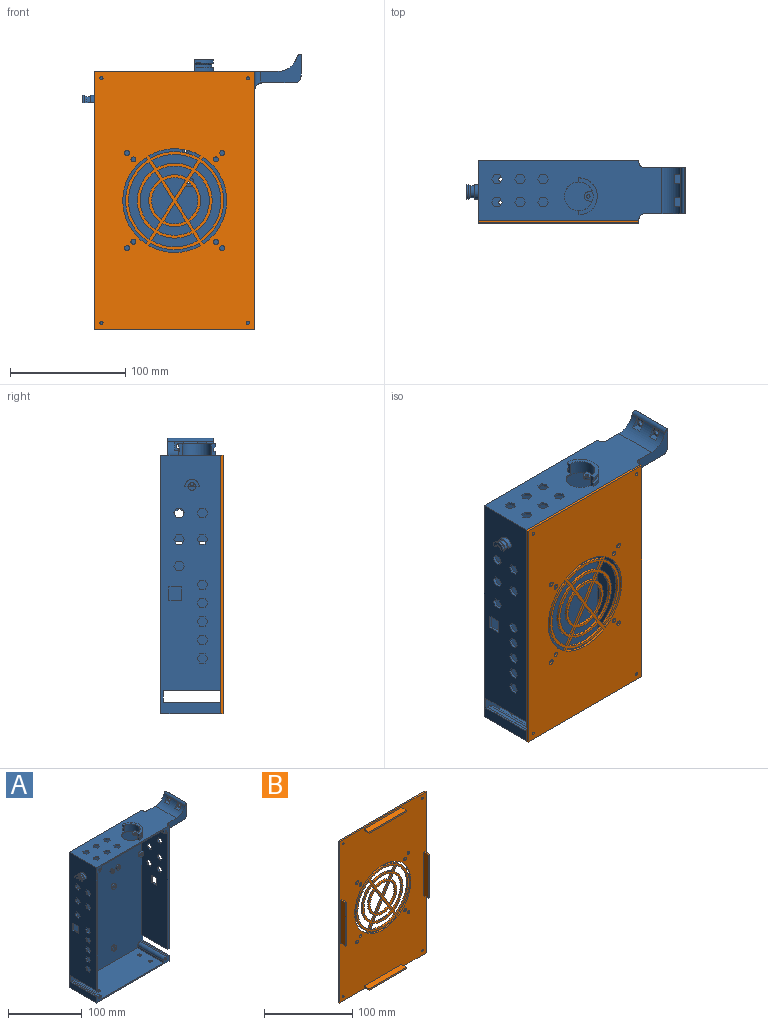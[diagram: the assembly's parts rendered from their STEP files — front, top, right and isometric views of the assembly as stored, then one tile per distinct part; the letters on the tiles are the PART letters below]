
ASSEMBLY  parts=2 mates=1
PART A: 292 faces, bbox 189x52x239 mm
  f0: cylinder r=17.13mm len=40mm, axis (0,-1,0), area 731mm2, adj f15,f134,f136,f139,f146,f147,f148,f149
  f1: plane 224x52mm, normal (1,0,0), area 9895.4mm2, adj f4,f7,f15,f16,f20,f21,f103,f104
  f2: plane 224x52mm, normal (-1,0,0), area 10383.8mm2, adj f4,f7,f11,f12,f15,f16,f20,f21
  f3: plane 193.92x50mm, normal (1,0,0), area 8938.3mm2, adj f16,f20,f28,f29,f32,f33,f36,f37
  f4: plane 224x139mm, normal (0,1,0), area 31065.2mm2, adj f1,f2,f15,f21,f22,f25,f31,f35
  f5: plane 50x0.08mm, normal (-1,0,0), area 3.8mm2, adj f7,f16,f70,f103
  f6: plane 50x0.08mm, normal (1,0,0), area 3.8mm2, adj f7,f16,f72,f105
  f7: plane 139x10.08mm, normal (0,-1,0), area 416.1mm2, adj f1,f2,f5,f6,f17,f21,f70,f71
  f8: cylinder r=3.25mm len=10mm, axis (-1,0,0), area 40.4mm2, adj f11,f96,f101,f102
  f9: cylinder r=3.25mm len=10mm, axis (-1,0,0), area 40.4mm2, adj f12,f96,f101,f102
  f10: cylinder r=6.25mm len=12.5mm, axis (1,0,0), area 33.7mm2, adj f11,f12,f96,f99
  f11: plane 10x3mm, normal (0,0,-1), area 26.3mm2, adj f2,f8,f10,f95,f96,f97,f98,f99
  f12: plane 10x3mm, normal (0,0,-1), area 26.3mm2, adj f2,f9,f10,f95,f96,f97,f98,f99
  f13: cylinder r=12.5mm len=25mm, axis (0,0,1), area 534.6mm2, adj f15,f19,f82,f83,f85,f89,f90,f91
  f14: cylinder r=16mm len=32mm, axis (0,0,-1), area 175.9mm2, adj f15,f82,f83,f86
  f15: plane 159x52mm, normal (0,0,1), area 7060.9mm2, adj f0,f1,f2,f4,f13,f14,f20,f82
  f16: plane 220x139mm, normal (0,-1,0), area 29004.3mm2, adj f1,f2,f3,f5,f6,f17,f18,f19
  f17: plane 119x50mm, normal (0,0,1), area 5871.5mm2, adj f7,f16,f71,f73,f288,f289,f290,f291
  f18: plane 193.92x50mm, normal (-1,0,0), area 9201.6mm2, adj f16,f20,f56,f59,f60,f61,f62,f65
  f19: plane 119x50mm, normal (0,0,-1), area 5173.4mm2, adj f13,f16,f20,f67,f69,f89,f90,f92
  f20: plane 203.92x139mm, normal (0,-1,0), area 1191.5mm2, adj f1,f2,f3,f15,f18,f19,f66,f67
  f21: plane 139x52mm, normal (0,0,-1), area 7149.5mm2, adj f1,f2,f4,f7,f288,f289,f290,f291
  f22: cylinder r=1.35mm len=5mm, axis (0,1,0), area 42.4mm2, adj f4,f24
  f23: cylinder r=4mm len=8mm, axis (0,1,0), area 75.4mm2, adj f16,f24
  f24: plane 8x8mm, normal (0,-1,0), area 44.5mm2, adj f22,f23
  f25: cylinder r=1.35mm len=5mm, axis (0,1,0), area 42.4mm2, adj f4,f27
  f26: cylinder r=4mm len=8mm, axis (0,1,0), area 75.4mm2, adj f16,f27
  f27: plane 8x8mm, normal (0,-1,0), area 44.5mm2, adj f25,f26
  f28: plane 5x3mm, normal (0,0,1), area 15mm2, adj f3,f16,f32,f128
  f29: plane 5x3mm, normal (0,0,-1), area 15mm2, adj f3,f16,f32,f129
  f30: plane 3x2mm, normal (1,0,0), area 6mm2, adj f16,f32,f128,f129
  f31: cylinder r=1.35mm len=5mm, axis (0,1,0), area 42.4mm2, adj f4,f32
  f32: plane 8x8mm, normal (0,-1,0), area 54.4mm2, adj f3,f28,f29,f30,f31,f128,f129
  f33: plane 5x3mm, normal (0,0,-1), area 15mm2, adj f3,f16,f37,f127
  f34: plane 3x2mm, normal (1,0,0), area 6mm2, adj f16,f37,f126,f127
  f35: cylinder r=1.35mm len=5mm, axis (0,1,0), area 42.4mm2, adj f4,f37
  f36: plane 5x3mm, normal (0,0,1), area 15mm2, adj f3,f16,f37,f126
  f37: plane 8x8mm, normal (0,-1,0), area 54.4mm2, adj f3,f33,f34,f35,f36,f126,f127
  f38: cylinder r=1.35mm len=5mm, axis (0,1,0), area 42.4mm2, adj f4,f40
  f39: cylinder r=3mm len=6mm, axis (0,1,0), area 56.5mm2, adj f16,f40
  f40: plane 6x6mm, normal (0,-1,0), area 22.5mm2, adj f38,f39
  f41: cylinder r=1.35mm len=5mm, axis (0,1,0), area 42.4mm2, adj f4,f43
  f42: cylinder r=3mm len=6mm, axis (0,1,0), area 56.5mm2, adj f16,f43
  f43: plane 6x6mm, normal (0,-1,0), area 22.5mm2, adj f41,f42
  f44: cylinder r=1.35mm len=5mm, axis (0,1,0), area 42.4mm2, adj f4,f46
  f45: cylinder r=3mm len=6mm, axis (0,1,0), area 56.5mm2, adj f16,f46
  f46: plane 6x6mm, normal (0,-1,0), area 22.5mm2, adj f44,f45
  f47: cylinder r=1.35mm len=5mm, axis (0,1,0), area 42.4mm2, adj f4,f49
  f48: cylinder r=3mm len=6mm, axis (0,1,0), area 56.5mm2, adj f16,f49
  f49: plane 6x6mm, normal (0,-1,0), area 22.5mm2, adj f47,f48
  f50: cylinder r=1.35mm len=5mm, axis (0,1,0), area 42.4mm2, adj f4,f52
  f51: cylinder r=3.5mm len=7mm, axis (0,1,0), area 66mm2, adj f16,f52
  f52: plane 7x7mm, normal (0,-1,0), area 32.8mm2, adj f50,f51
  f53: cylinder r=1.35mm len=5mm, axis (0,1,0), area 42.4mm2, adj f4,f55
  f54: cylinder r=3.5mm len=7mm, axis (0,1,0), area 66mm2, adj f16,f55
  f55: plane 7x7mm, normal (0,-1,0), area 32.8mm2, adj f53,f54
  f56: plane 4x3mm, normal (0,0,1), area 12mm2, adj f16,f18,f60,f125
  f57: plane 3x1mm, normal (-1,0,0), area 3mm2, adj f16,f60,f124,f125
  f58: cylinder r=1.35mm len=3mm, axis (0,1,0), area 25.4mm2, adj f60,f117
  f59: plane 4x3mm, normal (0,0,-1), area 12mm2, adj f16,f18,f60,f124
  f60: plane 7x7mm, normal (0,-1,0), area 39.4mm2, adj f18,f56,f57,f58,f59,f124,f125
  f61: plane 4x3mm, normal (0,0,-1), area 12mm2, adj f16,f18,f65,f122
  f62: plane 4x3mm, normal (0,0,1), area 12mm2, adj f16,f18,f65,f123
  f63: plane 3x1mm, normal (-1,0,0), area 3mm2, adj f16,f65,f122,f123
  f64: cylinder r=1.35mm len=5mm, axis (0,1,0), area 42.4mm2, adj f4,f65
  f65: plane 7x7mm, normal (0,-1,0), area 39.4mm2, adj f18,f61,f62,f63,f64,f122,f123
  f66: plane 50x3mm, normal (0,0,-1), area 150mm2, adj f3,f16,f20,f133
  f67: plane 50x3mm, normal (1,0,0), area 150mm2, adj f16,f19,f20,f133
  f68: plane 50x3mm, normal (0,0,-1), area 150mm2, adj f16,f18,f20,f132
  f69: plane 50x3mm, normal (-1,0,0), area 150mm2, adj f16,f19,f20,f132
  f70: plane 50x3mm, normal (0,0,1), area 150mm2, adj f5,f7,f16,f131
  f71: plane 50x3mm, normal (-1,0,0), area 150mm2, adj f7,f16,f17,f131
  f72: plane 50x3mm, normal (0,0,1), area 150mm2, adj f6,f7,f16,f130
  f73: plane 50x3mm, normal (1,0,0), area 150mm2, adj f7,f16,f17,f130
  f74: cylinder r=1.35mm len=25mm, axis (0,-1,0), area 212.1mm2, adj f20,f75
  f75: plane 2.7x2.7mm, normal (0,-1,0), area 5.7mm2, adj f74
  f76: cylinder r=1.35mm len=25mm, axis (0,-1,0), area 212.1mm2, adj f7,f77
  f77: plane 2.7x2.7mm, normal (0,-1,0), area 5.7mm2, adj f76
  f78: cylinder r=1.35mm len=25mm, axis (0,-1,0), area 212.1mm2, adj f7,f79
  f79: plane 2.7x2.7mm, normal (0,-1,0), area 5.7mm2, adj f78
  f80: cylinder r=1.35mm len=25mm, axis (0,-1,0), area 212.1mm2, adj f20,f81
  f81: plane 2.7x2.7mm, normal (0,-1,0), area 5.7mm2, adj f80
  f82: plane 10x3.5mm, normal (-1,0,0), area 30.3mm2, adj f13,f14,f15,f84,f85,f86,f87,f88
  f83: plane 10x3.5mm, normal (-1,0,0), area 30.3mm2, adj f13,f14,f15,f84,f85,f86,f87,f88
  f84: cylinder r=16mm len=32mm, axis (0,0,-1), area 134.9mm2, adj f82,f83,f85,f87
  f85: plane 32x16.14mm, normal (0,0,1), area 155.3mm2, adj f13,f82,f83,f84
  f86: plane 32x16.14mm, normal (0,0,1), area 70.2mm2, adj f14,f82,f83,f88
  f87: revolved ~32x16.2mm, area 93.7mm2, adj f82,f83,f84,f88
  f88: revolved ~29.04x14.72mm, area 114.2mm2, adj f82,f83,f86,f87
  f89: plane 3.05x2mm, normal (0,1,0), area 6.1mm2, adj f13,f19,f91,f93
  f90: plane 3.05x2mm, normal (0,-1,0), area 6.1mm2, adj f13,f19,f91,f93
  f91: plane 8x7.71mm, normal (0,0,1), area 46mm2, adj f13,f89,f90,f92,f93
  f92: cylinder r=1.5mm len=3mm, axis (0,0,1), area 18.8mm2, adj f19,f91
  f93: cylinder r=4mm len=8mm, axis (0,0,1), area 25.1mm2, adj f19,f89,f90,f91
  f94: cylinder r=3.25mm len=6.5mm, axis (-1,0,0), area 20.4mm2, adj f2,f3,f100
  f95: cylinder r=6.25mm len=12.5mm, axis (1,0,0), area 73.6mm2, adj f2,f11,f12,f97
  f96: plane 12.5x6.25mm, normal (-1,0,0), area 44.4mm2, adj f8,f9,f10,f11,f12,f101
  f97: plane 12.5x6.25mm, normal (-1,0,0), area 18.1mm2, adj f11,f12,f95,f98
  f98: cylinder r=5.25mm len=10.5mm, axis (1,0,0), area 46.2mm2, adj f11,f12,f97,f99
  f99: cone r=5.25mm half-angle=30deg, axis (-1,0,0), area 36.1mm2, adj f10,f11,f12,f98
  f100: plane 6.5x2mm, normal (0,0,-1), area 13mm2, adj f3,f94,f102
  f101: cylinder r=1.5mm len=12mm, axis (-1,0,0), area 41.9mm2, adj f3,f8,f9,f96,f102
  f102: plane 6.5x3.08mm, normal (-1,0,0), area 9.9mm2, adj f8,f9,f100,f101
  f103: plane 50x2mm, normal (0,0,1), area 100mm2, adj f1,f5,f7,f16
  f104: plane 50x2mm, normal (0,0,-1), area 100mm2, adj f1,f16,f18,f20
  f105: plane 50x2mm, normal (0,0,1), area 100mm2, adj f2,f6,f7,f16
  f106: plane 50x2mm, normal (0,0,-1), area 100mm2, adj f2,f3,f16,f20
  f107: plane 12x2mm, normal (0,1,0), area 24mm2, adj f1,f18,f108,f110
  f108: plane 10x2mm, normal (0,0,1), area 20mm2, adj f1,f18,f107,f109
  f109: plane 12x2mm, normal (0,-1,0), area 24mm2, adj f1,f18,f108,f110
  f110: plane 10x2mm, normal (0,0,-1), area 20mm2, adj f1,f18,f107,f109
  f111: plane 2x1.71mm, normal (-0.17,0,0.99), area 3.5mm2, adj f4,f112,f116,f117
  f112: plane 2x1.63mm, normal (-0.94,0,0.35), area 3.5mm2, adj f4,f111,f113,f117
  f113: plane 2x1.33mm, normal (-0.77,0,-0.64), area 3.5mm2, adj f4,f112,f114,f117
  f114: plane 2x1.71mm, normal (0.17,0,-0.99), area 3.5mm2, adj f4,f113,f115,f117
  f115: plane 2x1.63mm, normal (0.94,0,-0.35), area 3.5mm2, adj f4,f114,f116,f117
  f116: plane 2x1.33mm, normal (0.77,0,0.64), area 3.5mm2, adj f4,f111,f115,f117
  f117: plane 3.41x3.25mm, normal (0,1,0), area 2.1mm2, adj f58,f111,f112,f113,f114,f115,f116
  f118: plane 12x2mm, normal (0,-1,0), area 24mm2, adj f2,f3,f119,f121
  f119: plane 11x2mm, normal (0,0,1), area 22mm2, adj f2,f3,f118,f120
  f120: plane 12x2mm, normal (0,1,0), area 24mm2, adj f2,f3,f119,f121
  f121: plane 11x2mm, normal (0,0,-1), area 22mm2, adj f2,f3,f118,f120
  f122: cylinder r=3mm len=3mm, axis (0,1,0), area 14.1mm2, adj f16,f61,f63,f65
  f123: cylinder r=3mm len=3mm, axis (0,-1,0), area 14.1mm2, adj f16,f62,f63,f65
  f124: cylinder r=3mm len=3mm, axis (0,-1,0), area 14.1mm2, adj f16,f57,f59,f60
  f125: cylinder r=3mm len=3mm, axis (0,1,0), area 14.1mm2, adj f16,f56,f57,f60
  f126: cylinder r=3mm len=3mm, axis (0,-1,0), area 14.1mm2, adj f16,f34,f36,f37
  f127: cylinder r=3mm len=3mm, axis (0,1,0), area 14.1mm2, adj f16,f33,f34,f37
  f128: cylinder r=3mm len=3mm, axis (0,1,0), area 14.1mm2, adj f16,f28,f30,f32
  f129: cylinder r=3mm len=3mm, axis (0,-1,0), area 14.1mm2, adj f16,f29,f30,f32
  f130: cylinder r=5mm len=50mm, axis (0,-1,0), area 392.7mm2, adj f7,f16,f72,f73
  f131: cylinder r=5mm len=50mm, axis (0,-1,0), area 392.7mm2, adj f7,f16,f70,f71
  f132: cylinder r=5mm len=50mm, axis (0,-1,0), area 392.7mm2, adj f16,f20,f68,f69
  f133: cylinder r=5mm len=50mm, axis (0,-1,0), area 392.7mm2, adj f16,f20,f66,f67
  f134: plane 35x25.08mm, normal (0,-1,0), area 446.7mm2, adj f0,f15,f135,f137,f138,f139,f140,f141
  f135: plane 40x28mm, normal (0,0,-1), area 1120mm2, adj f134,f136,f140,f141
  f136: plane 35x25.08mm, normal (0,1,0), area 446.7mm2, adj f0,f15,f135,f137,f138,f139,f140,f141
  f137: plane 40x19mm, normal (1,0,0), area 720.7mm2, adj f134,f136,f138,f141,f144,f145
  f138: plane 40x0.15mm, normal (0,0,1), area 6mm2, adj f134,f136,f137,f139
  f139: cylinder r=3.5mm len=40mm, axis (0,-1,0), area 181.2mm2, adj f0,f134,f136,f138
  f140: cylinder r=6mm len=50mm, axis (0,1,0), area 408.1mm2, adj f1,f134,f135,f136,f142,f143
  f141: cylinder r=6mm len=40mm, axis (0,-1,0), area 377mm2, adj f134,f135,f136,f137
  f142: cylinder r=5mm len=16mm, axis (0,0,-1), area 97.4mm2, adj f1,f15,f134,f140
  f143: cylinder r=5mm len=16mm, axis (0,0,1), area 97.4mm2, adj f1,f15,f136,f140
  f144: cylinder r=2.5mm len=5mm, axis (1,0,0), area 55mm2, adj f137,f155
  f145: cylinder r=2.5mm len=5mm, axis (1,0,0), area 55mm2, adj f137,f150
  f146: plane 8x0.15mm, normal (0,0,-1), area 1.2mm2, adj f0,f147,f149,f150
  f147: plane 8x5.5mm, normal (0,1,0), area 18.2mm2, adj f0,f146,f148,f150
  f148: plane 8x5.5mm, normal (0,0,1), area 44mm2, adj f0,f147,f149,f150
  f149: plane 8x5.5mm, normal (0,-1,0), area 18.2mm2, adj f0,f146,f148,f150
  f150: plane 8x8mm, normal (-1,0,0), area 44.4mm2, adj f145,f146,f147,f148,f149
  f151: plane 8x0.15mm, normal (0,0,-1), area 1.2mm2, adj f0,f152,f154,f155
  f152: plane 8x5.5mm, normal (0,1,0), area 18.2mm2, adj f0,f151,f153,f155
  f153: plane 8x5.5mm, normal (0,0,1), area 44mm2, adj f0,f152,f154,f155
  f154: plane 8x5.5mm, normal (0,-1,0), area 18.2mm2, adj f0,f151,f153,f155
  f155: plane 8x8mm, normal (-1,0,0), area 44.4mm2, adj f144,f151,f152,f153,f154
  f156: plane 4.62x2mm, normal (0,0,-1), area 9.2mm2, adj f1,f18,f157,f161
  f157: plane 4x2.31mm, normal (0,0.87,-0.5), area 9.2mm2, adj f1,f18,f156,f158
  f158: plane 4x2.31mm, normal (0,0.87,0.5), area 9.2mm2, adj f1,f18,f157,f159
  f159: plane 4.62x2mm, normal (0,0,1), area 9.2mm2, adj f1,f18,f158,f160
  f160: plane 4x2.31mm, normal (0,-0.87,0.5), area 9.2mm2, adj f1,f18,f159,f161
  f161: plane 4x2.31mm, normal (0,-0.87,-0.5), area 9.2mm2, adj f1,f18,f156,f160
  f162: plane 4.62x2mm, normal (0,0,-1), area 9.2mm2, adj f1,f18,f163,f167
  f163: plane 4x2.31mm, normal (0,0.87,-0.5), area 9.2mm2, adj f1,f18,f162,f164
  f164: plane 4x2.31mm, normal (0,0.87,0.5), area 9.2mm2, adj f1,f18,f163,f165
  f165: plane 4.62x2mm, normal (0,0,1), area 9.2mm2, adj f1,f18,f164,f166
  f166: plane 4x2.31mm, normal (0,-0.87,0.5), area 9.2mm2, adj f1,f18,f165,f167
  f167: plane 4x2.31mm, normal (0,-0.87,-0.5), area 9.2mm2, adj f1,f18,f162,f166
  f168: plane 4.62x2mm, normal (0,0,-1), area 9.2mm2, adj f1,f18,f169,f173
  f169: plane 4x2.31mm, normal (0,0.87,-0.5), area 9.2mm2, adj f1,f18,f168,f170
  f170: plane 4x2.31mm, normal (0,0.87,0.5), area 9.2mm2, adj f1,f18,f169,f171
  f171: plane 4.62x2mm, normal (0,0,1), area 9.2mm2, adj f1,f18,f170,f172
  f172: plane 4x2.31mm, normal (0,-0.87,0.5), area 9.2mm2, adj f1,f18,f171,f173
  f173: plane 4x2.31mm, normal (0,-0.87,-0.5), area 9.2mm2, adj f1,f18,f168,f172
  f174: plane 4.62x2mm, normal (0,0,-1), area 9.2mm2, adj f1,f18,f175,f179
  f175: plane 4x2.31mm, normal (0,0.87,-0.5), area 9.2mm2, adj f1,f18,f174,f176
  f176: plane 4x2.31mm, normal (0,0.87,0.5), area 9.2mm2, adj f1,f18,f175,f177
  f177: plane 4.62x2mm, normal (0,0,1), area 9.2mm2, adj f1,f18,f176,f178
  f178: plane 4x2.31mm, normal (0,-0.87,0.5), area 9.2mm2, adj f1,f18,f177,f179
  f179: plane 4x2.31mm, normal (0,-0.87,-0.5), area 9.2mm2, adj f1,f18,f174,f178
  f180: plane 4x2.31mm, normal (0,0.5,-0.87), area 9.2mm2, adj f1,f18,f181,f185
  f181: plane 4.62x2mm, normal (0,1,0), area 9.2mm2, adj f1,f18,f180,f182
  f182: plane 4x2.31mm, normal (0,0.5,0.87), area 9.2mm2, adj f1,f18,f181,f183
  f183: plane 4x2.31mm, normal (0,-0.5,0.87), area 9.2mm2, adj f1,f18,f182,f184
  f184: plane 4.62x2mm, normal (0,-1,0), area 9.2mm2, adj f1,f18,f183,f185
  f185: plane 4x2.31mm, normal (0,-0.5,-0.87), area 9.2mm2, adj f1,f18,f180,f184
  f186: plane 4.62x2mm, normal (0,0,-1), area 9.2mm2, adj f1,f18,f187,f191
  f187: plane 4x2.31mm, normal (0,0.87,-0.5), area 9.2mm2, adj f1,f18,f186,f188
  f188: plane 4x2.31mm, normal (0,0.87,0.5), area 9.2mm2, adj f1,f18,f187,f189
  f189: plane 4.62x2mm, normal (0,0,1), area 9.2mm2, adj f1,f18,f188,f190
  f190: plane 4x2.31mm, normal (0,-0.87,0.5), area 9.2mm2, adj f1,f18,f189,f191
  f191: plane 4x2.31mm, normal (0,-0.87,-0.5), area 9.2mm2, adj f1,f18,f186,f190
  f192: plane 4.62x2mm, normal (0,0,-1), area 9.2mm2, adj f2,f3,f193,f197
  f193: plane 4x2.31mm, normal (0,-0.87,-0.5), area 9.2mm2, adj f2,f3,f192,f194
  f194: plane 4x2.31mm, normal (0,-0.87,0.5), area 9.2mm2, adj f2,f3,f193,f195
  f195: plane 4.62x2mm, normal (0,0,1), area 9.2mm2, adj f2,f3,f194,f196
  f196: plane 4x2.31mm, normal (0,0.87,0.5), area 9.2mm2, adj f2,f3,f195,f197
  f197: plane 4x2.31mm, normal (0,0.87,-0.5), area 9.2mm2, adj f2,f3,f192,f196
  f198: plane 4.62x2mm, normal (0,0,-1), area 9.2mm2, adj f2,f3,f199,f203
  f199: plane 4x2.31mm, normal (0,-0.87,-0.5), area 9.2mm2, adj f2,f3,f198,f200
  f200: plane 4x2.31mm, normal (0,-0.87,0.5), area 9.2mm2, adj f2,f3,f199,f201
  f201: plane 4.62x2mm, normal (0,0,1), area 9.2mm2, adj f2,f3,f200,f202
  f202: plane 4x2.31mm, normal (0,0.87,0.5), area 9.2mm2, adj f2,f3,f201,f203
  f203: plane 4x2.31mm, normal (0,0.87,-0.5), area 9.2mm2, adj f2,f3,f198,f202
  f204: plane 4.62x2mm, normal (0,0,-1), area 9.2mm2, adj f2,f3,f205,f209
  f205: plane 4x2.31mm, normal (0,-0.87,-0.5), area 9.2mm2, adj f2,f3,f204,f206
  f206: plane 4x2.31mm, normal (0,-0.87,0.5), area 9.2mm2, adj f2,f3,f205,f207
  f207: plane 4.62x2mm, normal (0,0,1), area 9.2mm2, adj f2,f3,f206,f208
  f208: plane 4x2.31mm, normal (0,0.87,0.5), area 9.2mm2, adj f2,f3,f207,f209
  f209: plane 4x2.31mm, normal (0,0.87,-0.5), area 9.2mm2, adj f2,f3,f204,f208
  f210: plane 4.62x2mm, normal (0,0,-1), area 9.2mm2, adj f2,f3,f211,f215
  f211: plane 4x2.31mm, normal (0,-0.87,-0.5), area 9.2mm2, adj f2,f3,f210,f212
  f212: plane 4x2.31mm, normal (0,-0.87,0.5), area 9.2mm2, adj f2,f3,f211,f213
  f213: plane 4.62x2mm, normal (0,0,1), area 9.2mm2, adj f2,f3,f212,f214
  f214: plane 4x2.31mm, normal (0,0.87,0.5), area 9.2mm2, adj f2,f3,f213,f215
  f215: plane 4x2.31mm, normal (0,0.87,-0.5), area 9.2mm2, adj f2,f3,f210,f214
  f216: plane 4.62x2mm, normal (0,0,-1), area 9.2mm2, adj f2,f3,f217,f221
  f217: plane 4x2.31mm, normal (0,-0.87,-0.5), area 9.2mm2, adj f2,f3,f216,f218
  f218: plane 4x2.31mm, normal (0,-0.87,0.5), area 9.2mm2, adj f2,f3,f217,f219
  f219: plane 4.62x2mm, normal (0,0,1), area 9.2mm2, adj f2,f3,f218,f220
  f220: plane 4x2.31mm, normal (0,0.87,0.5), area 9.2mm2, adj f2,f3,f219,f221
  f221: plane 4x2.31mm, normal (0,0.87,-0.5), area 9.2mm2, adj f2,f3,f216,f220
  f222: plane 4.62x2mm, normal (0,0,-1), area 9.2mm2, adj f2,f3,f223,f227
  f223: plane 4x2.31mm, normal (0,-0.87,-0.5), area 9.2mm2, adj f2,f3,f222,f224
  f224: plane 4x2.31mm, normal (0,-0.87,0.5), area 9.2mm2, adj f2,f3,f223,f225
  f225: plane 4.62x2mm, normal (0,0,1), area 9.2mm2, adj f2,f3,f224,f226
  f226: plane 4x2.31mm, normal (0,0.87,0.5), area 9.2mm2, adj f2,f3,f225,f227
  f227: plane 4x2.31mm, normal (0,0.87,-0.5), area 9.2mm2, adj f2,f3,f222,f226
  f228: plane 4.62x2mm, normal (0,0,-1), area 9.2mm2, adj f2,f3,f229,f233
  f229: plane 4x2.31mm, normal (0,-0.87,-0.5), area 9.2mm2, adj f2,f3,f228,f230
  f230: plane 4x2.31mm, normal (0,-0.87,0.5), area 9.2mm2, adj f2,f3,f229,f231
  f231: plane 4.62x2mm, normal (0,0,1), area 9.2mm2, adj f2,f3,f230,f232
  f232: plane 4x2.31mm, normal (0,0.87,0.5), area 9.2mm2, adj f2,f3,f231,f233
  f233: plane 4x2.31mm, normal (0,0.87,-0.5), area 9.2mm2, adj f2,f3,f228,f232
  f234: plane 4.62x2mm, normal (0,0,-1), area 9.2mm2, adj f2,f3,f235,f239
  f235: plane 4x2.31mm, normal (0,-0.87,-0.5), area 9.2mm2, adj f2,f3,f234,f236
  f236: plane 4x2.31mm, normal (0,-0.87,0.5), area 9.2mm2, adj f2,f3,f235,f237
  f237: plane 4.62x2mm, normal (0,0,1), area 9.2mm2, adj f2,f3,f236,f238
  f238: plane 4x2.31mm, normal (0,0.87,0.5), area 9.2mm2, adj f2,f3,f237,f239
  f239: plane 4x2.31mm, normal (0,0.87,-0.5), area 9.2mm2, adj f2,f3,f234,f238
  f240: plane 4.62x2mm, normal (0,0,-1), area 9.2mm2, adj f2,f3,f241,f245
  f241: plane 4x2.31mm, normal (0,-0.87,-0.5), area 9.2mm2, adj f2,f3,f240,f242
  f242: plane 4x2.31mm, normal (0,-0.87,0.5), area 9.2mm2, adj f2,f3,f241,f243
  f243: plane 4.62x2mm, normal (0,0,1), area 9.2mm2, adj f2,f3,f242,f244
  f244: plane 4x2.31mm, normal (0,0.87,0.5), area 9.2mm2, adj f2,f3,f243,f245
  f245: plane 4x2.31mm, normal (0,0.87,-0.5), area 9.2mm2, adj f2,f3,f240,f244
  f246: plane 4.62x2mm, normal (0,0,-1), area 9.2mm2, adj f2,f3,f247,f251
  f247: plane 4x2.31mm, normal (0,-0.87,-0.5), area 9.2mm2, adj f2,f3,f246,f248
  f248: plane 4x2.31mm, normal (0,-0.87,0.5), area 9.2mm2, adj f2,f3,f247,f249
  f249: plane 4.62x2mm, normal (0,0,1), area 9.2mm2, adj f2,f3,f248,f250
  f250: plane 4x2.31mm, normal (0,0.87,0.5), area 9.2mm2, adj f2,f3,f249,f251
  f251: plane 4x2.31mm, normal (0,0.87,-0.5), area 9.2mm2, adj f2,f3,f246,f250
  f252: plane 4.58x2mm, normal (0,-1,0), area 9.2mm2, adj f15,f19,f253,f257
  f253: plane 3.97x2.29mm, normal (0.87,-0.5,0), area 9.2mm2, adj f15,f19,f252,f254
  f254: plane 3.97x2.29mm, normal (0.87,0.5,0), area 9.2mm2, adj f15,f19,f253,f255
  f255: plane 4.58x2mm, normal (0,1,0), area 9.2mm2, adj f15,f19,f254,f256
  f256: plane 3.97x2.29mm, normal (-0.87,0.5,0), area 9.2mm2, adj f15,f19,f255,f257
  f257: plane 3.97x2.29mm, normal (-0.87,-0.5,0), area 9.2mm2, adj f15,f19,f252,f256
  f258: plane 4x2.31mm, normal (-0.87,-0.5,0), area 9.2mm2, adj f15,f19,f259,f263
  f259: plane 4.62x2mm, normal (0,-1,0), area 9.2mm2, adj f15,f19,f258,f260
  f260: plane 4x2.31mm, normal (0.87,-0.5,0), area 9.2mm2, adj f15,f19,f259,f261
  f261: plane 4x2.31mm, normal (0.87,0.5,0), area 9.2mm2, adj f15,f19,f260,f262
  f262: plane 4.62x2mm, normal (0,1,0), area 9.2mm2, adj f15,f19,f261,f263
  f263: plane 4x2.31mm, normal (-0.87,0.5,0), area 9.2mm2, adj f15,f19,f258,f262
  f264: plane 4.62x2mm, normal (0,-1,0), area 9.2mm2, adj f15,f19,f265,f269
  f265: plane 4x2.31mm, normal (0.87,-0.5,0), area 9.2mm2, adj f15,f19,f264,f266
  f266: plane 4x2.31mm, normal (0.87,0.5,0), area 9.2mm2, adj f15,f19,f265,f267
  f267: plane 4.62x2mm, normal (0,1,0), area 9.2mm2, adj f15,f19,f266,f268
  f268: plane 4x2.31mm, normal (-0.87,0.5,0), area 9.2mm2, adj f15,f19,f267,f269
  f269: plane 4x2.31mm, normal (-0.87,-0.5,0), area 9.2mm2, adj f15,f19,f264,f268
  f270: plane 4x2.31mm, normal (-0.87,-0.5,0), area 9.2mm2, adj f15,f19,f271,f275
  f271: plane 4.62x2mm, normal (0,-1,0), area 9.2mm2, adj f15,f19,f270,f272
  f272: plane 4x2.31mm, normal (0.87,-0.5,0), area 9.2mm2, adj f15,f19,f271,f273
  f273: plane 4x2.31mm, normal (0.87,0.5,0), area 9.2mm2, adj f15,f19,f272,f274
  f274: plane 4.62x2mm, normal (0,1,0), area 9.2mm2, adj f15,f19,f273,f275
  f275: plane 4x2.31mm, normal (-0.87,0.5,0), area 9.2mm2, adj f15,f19,f270,f274
  f276: plane 4.62x2mm, normal (0,-1,0), area 9.2mm2, adj f15,f19,f277,f281
  f277: plane 4x2.31mm, normal (0.87,-0.5,0), area 9.2mm2, adj f15,f19,f276,f278
  f278: plane 4x2.31mm, normal (0.87,0.5,0), area 9.2mm2, adj f15,f19,f277,f279
  f279: plane 4.62x2mm, normal (0,1,0), area 9.2mm2, adj f15,f19,f278,f280
  f280: plane 4x2.31mm, normal (-0.87,0.5,0), area 9.2mm2, adj f15,f19,f279,f281
  f281: plane 4x2.31mm, normal (-0.87,-0.5,0), area 9.2mm2, adj f15,f19,f276,f280
  f282: plane 4x2.31mm, normal (-0.87,0.5,0), area 9.2mm2, adj f15,f19,f283,f287
  f283: plane 4x2.31mm, normal (-0.87,-0.5,0), area 9.2mm2, adj f15,f19,f282,f284
  f284: plane 4.62x2mm, normal (0,-1,0), area 9.2mm2, adj f15,f19,f283,f285
  f285: plane 4x2.31mm, normal (0.87,-0.5,0), area 9.2mm2, adj f15,f19,f284,f286
  f286: plane 4x2.31mm, normal (0.87,0.5,0), area 9.2mm2, adj f15,f19,f285,f287
  f287: plane 4.62x2mm, normal (0,1,0), area 9.2mm2, adj f15,f19,f282,f286
  f288: cylinder r=2.5mm len=5mm, axis (0,0,-1), area 31.4mm2, adj f17,f21
  f289: cylinder r=2.5mm len=5mm, axis (0,0,-1), area 31.4mm2, adj f17,f21
  f290: cylinder r=2.5mm len=5mm, axis (0,0,-1), area 31.4mm2, adj f17,f21
  f291: cylinder r=2.5mm len=5mm, axis (0,0,-1), area 31.4mm2, adj f17,f21
PART B: 98 faces, bbox 139x10x224 mm
  f0: plane 224x139mm, normal (0,-1,0), area 26032.1mm2, adj f2,f3,f4,f5,f6,f7,f8,f9
  f1: plane 224x139mm, normal (0,1,0), area 26512.1mm2, adj f2,f3,f4,f5,f6,f7,f8,f9
  f2: plane 139x2mm, normal (0,0,1), area 278mm2, adj f0,f1,f3,f5
  f3: plane 224x2mm, normal (-1,0,0), area 448mm2, adj f0,f1,f2,f4
  f4: plane 139x2mm, normal (0,0,-1), area 278mm2, adj f0,f1,f3,f5
  f5: plane 224x2mm, normal (1,0,0), area 448mm2, adj f0,f1,f2,f4
  f6: cylinder r=1.35mm len=2.7mm, axis (0,-1,0), area 17mm2, adj f0,f1
  f7: cylinder r=1.35mm len=2.7mm, axis (0,-1,0), area 17mm2, adj f0,f1
  f8: cylinder r=1.35mm len=2.7mm, axis (0,-1,0), area 17mm2, adj f0,f1
  f9: cylinder r=1.35mm len=2.7mm, axis (0,-1,0), area 17mm2, adj f0,f1
  f10: plane 60x8mm, normal (0,0,1), area 480mm2, adj f0,f11,f13,f14
  f11: plane 8x2mm, normal (-1,0,0), area 16mm2, adj f0,f10,f12,f14
  f12: plane 60x8mm, normal (0,0,-1), area 480mm2, adj f0,f11,f13,f14
  f13: plane 8x2mm, normal (1,0,0), area 16mm2, adj f0,f10,f12,f14
  f14: plane 60x2mm, normal (0,-1,0), area 120mm2, adj f10,f11,f12,f13
  f15: plane 60x8mm, normal (-1,0,0), area 480mm2, adj f0,f16,f18,f19
  f16: plane 8x2mm, normal (0,0,-1), area 16mm2, adj f0,f15,f17,f19
  f17: plane 60x8mm, normal (1,0,0), area 480mm2, adj f0,f16,f18,f19
  f18: plane 8x2mm, normal (0,0,1), area 16mm2, adj f0,f15,f17,f19
  f19: plane 60x2mm, normal (0,-1,0), area 120mm2, adj f15,f16,f17,f18
  f20: plane 60x8mm, normal (0,0,1), area 480mm2, adj f0,f21,f23,f24
  f21: plane 8x2mm, normal (-1,0,0), area 16mm2, adj f0,f20,f22,f24
  f22: plane 60x8mm, normal (0,0,-1), area 480mm2, adj f0,f21,f23,f24
  f23: plane 8x2mm, normal (1,0,0), area 16mm2, adj f0,f20,f22,f24
  f24: plane 60x2mm, normal (0,-1,0), area 120mm2, adj f20,f21,f22,f23
  f25: plane 8x2mm, normal (0,0,-1), area 16mm2, adj f0,f26,f28,f29
  f26: plane 60x8mm, normal (1,0,0), area 480mm2, adj f0,f25,f27,f29
  f27: plane 8x2mm, normal (0,0,1), area 16mm2, adj f0,f26,f28,f29
  f28: plane 60x8mm, normal (-1,0,0), area 480mm2, adj f0,f25,f27,f29
  f29: plane 60x2mm, normal (0,-1,0), area 120mm2, adj f25,f26,f27,f28
  f30: cylinder r=2.15mm len=4.3mm, axis (0,-1,0), area 27mm2, adj f0,f1
  f31: cylinder r=32.5mm len=53.82mm, axis (0,-1,0), area 126.8mm2, adj f0,f1,f32,f34
  f32: plane 6.39x3.94mm, normal (0.85,0,0.53), area 15mm2, adj f0,f1,f31,f33
  f33: cylinder r=40mm len=66.59mm, axis (0,-1,0), area 157.4mm2, adj f0,f1,f32,f34
  f34: plane 6.39x3.94mm, normal (0.85,0,-0.53), area 15mm2, adj f0,f1,f31,f33
  f35: cylinder r=42.5mm len=70.85mm, axis (0,-1,0), area 167.5mm2, adj f0,f1,f36,f38
  f36: plane 2.13x2mm, normal (0.85,0,0.53), area 5mm2, adj f0,f1,f35,f37
  f37: cylinder r=45mm len=75.11mm, axis (0,-1,0), area 177.7mm2, adj f0,f1,f36,f38
  f38: plane 2.13x2mm, normal (0.85,0,-0.53), area 5mm2, adj f0,f1,f35,f37
  f39: plane 6.39x3.94mm, normal (-0.85,0,0.53), area 15mm2, adj f0,f1,f40,f42
  f40: cylinder r=30mm len=29.13mm, axis (0,-1,0), area 60.8mm2, adj f0,f1,f39,f41
  f41: plane 6.39x3.94mm, normal (0.85,0,0.53), area 15mm2, adj f0,f1,f40,f42
  f42: cylinder r=22.5mm len=21.25mm, axis (0,-1,0), area 44.3mm2, adj f0,f1,f39,f41
  f43: cylinder r=22.5mm len=36.78mm, axis (0,-1,0), area 86.1mm2, adj f0,f1,f44,f46
  f44: plane 6.39x3.94mm, normal (0.85,0,0.53), area 15mm2, adj f0,f1,f43,f45
  f45: cylinder r=30mm len=49.56mm, axis (0,-1,0), area 116.6mm2, adj f0,f1,f44,f46
  f46: plane 6.39x3.94mm, normal (0.85,0,-0.53), area 15mm2, adj f0,f1,f43,f45
  f47: plane 6.39x3.94mm, normal (0.85,0,-0.53), area 15mm2, adj f0,f1,f48,f50
  f48: cylinder r=30mm len=29.13mm, axis (0,-1,0), area 60.8mm2, adj f0,f1,f47,f49
  f49: plane 6.39x3.94mm, normal (-0.85,0,-0.53), area 15mm2, adj f0,f1,f48,f50
  f50: cylinder r=22.5mm len=21.25mm, axis (0,-1,0), area 44.3mm2, adj f0,f1,f47,f49
  f51: plane 2.13x2mm, normal (0.85,0,-0.53), area 5mm2, adj f0,f1,f52,f54
  f52: cylinder r=45mm len=44.9mm, axis (0,-1,0), area 94mm2, adj f0,f1,f51,f53
  f53: plane 2.13x2mm, normal (-0.85,0,-0.53), area 5mm2, adj f0,f1,f52,f54
  f54: cylinder r=42.5mm len=42.27mm, axis (0,-1,0), area 88.5mm2, adj f0,f1,f51,f53
  f55: plane 6.39x3.94mm, normal (0.85,0,-0.53), area 15mm2, adj f0,f1,f56,f58
  f56: cylinder r=40mm len=39.65mm, axis (0,-1,0), area 83mm2, adj f0,f1,f55,f57
  f57: plane 6.39x3.94mm, normal (-0.85,0,-0.53), area 15mm2, adj f0,f1,f56,f58
  f58: cylinder r=32.5mm len=31.76mm, axis (0,-1,0), area 66.4mm2, adj f0,f1,f55,f57
  f59: cylinder r=2.15mm len=4.3mm, axis (0,-1,0), area 27mm2, adj f0,f1
  f60: cylinder r=2.15mm len=4.3mm, axis (0,-1,0), area 27mm2, adj f0,f1
  f61: cylinder r=2.15mm len=4.3mm, axis (0,-1,0), area 27mm2, adj f0,f1
  f62: plane 16.26x10.03mm, normal (-0.85,0,-0.53), area 38.2mm2, adj f0,f1,f63,f64
  f63: cylinder r=20mm len=32.51mm, axis (0,-1,0), area 75.9mm2, adj f0,f1,f62,f64
  f64: plane 16.26x10.03mm, normal (-0.85,0,0.53), area 38.2mm2, adj f0,f1,f62,f63
  f65: cylinder r=2.15mm len=4.3mm, axis (0,-1,0), area 27mm2, adj f0,f1
  f66: cylinder r=2.15mm len=4.3mm, axis (0,-1,0), area 27mm2, adj f0,f1
  f67: cylinder r=2.15mm len=4.3mm, axis (0,-1,0), area 27mm2, adj f0,f1
  f68: cylinder r=2.15mm len=4.3mm, axis (0,-1,0), area 27mm2, adj f0,f1
  f69: plane 2.13x2mm, normal (-0.85,0,-0.53), area 5mm2, adj f0,f1,f70,f72
  f70: cylinder r=45mm len=75.11mm, axis (0,-1,0), area 177.7mm2, adj f0,f1,f69,f71
  f71: plane 2.13x2mm, normal (-0.85,0,0.53), area 5mm2, adj f0,f1,f70,f72
  f72: cylinder r=42.5mm len=70.85mm, axis (0,-1,0), area 167.5mm2, adj f0,f1,f69,f71
  f73: plane 6.39x3.94mm, normal (-0.85,0,-0.53), area 15mm2, adj f0,f1,f74,f76
  f74: cylinder r=40mm len=66.59mm, axis (0,-1,0), area 157.4mm2, adj f0,f1,f73,f75
  f75: plane 6.39x3.94mm, normal (-0.85,0,0.53), area 15mm2, adj f0,f1,f74,f76
  f76: cylinder r=32.5mm len=53.82mm, axis (0,-1,0), area 126.8mm2, adj f0,f1,f73,f75
  f77: plane 6.39x3.94mm, normal (-0.85,0,0.53), area 15mm2, adj f0,f1,f78,f80
  f78: cylinder r=40mm len=39.65mm, axis (0,-1,0), area 83mm2, adj f0,f1,f77,f79
  f79: plane 6.39x3.94mm, normal (0.85,0,0.53), area 15mm2, adj f0,f1,f78,f80
  f80: cylinder r=32.5mm len=31.76mm, axis (0,-1,0), area 66.4mm2, adj f0,f1,f77,f79
  f81: plane 2.13x2mm, normal (-0.85,0,0.53), area 5mm2, adj f0,f1,f82,f84
  f82: cylinder r=45mm len=44.9mm, axis (0,-1,0), area 94mm2, adj f0,f1,f81,f83
  f83: plane 2.13x2mm, normal (0.85,0,0.53), area 5mm2, adj f0,f1,f82,f84
  f84: cylinder r=42.5mm len=42.27mm, axis (0,-1,0), area 88.5mm2, adj f0,f1,f81,f83
  f85: plane 16.26x10.03mm, normal (0.85,0,-0.53), area 38.2mm2, adj f0,f1,f86,f87
  f86: plane 16.26x10.03mm, normal (0.85,0,0.53), area 38.2mm2, adj f0,f1,f85,f87
  f87: cylinder r=20mm len=32.51mm, axis (0,-1,0), area 75.9mm2, adj f0,f1,f85,f86
  f88: plane 15.08x9.31mm, normal (-0.85,0,0.53), area 35.4mm2, adj f0,f1,f89,f90
  f89: cylinder r=20mm len=18.61mm, axis (0,-1,0), area 38.7mm2, adj f0,f1,f88,f90
  f90: plane 15.08x9.31mm, normal (0.85,0,0.53), area 35.4mm2, adj f0,f1,f88,f89
  f91: plane 15.08x9.31mm, normal (-0.85,0,-0.53), area 35.4mm2, adj f0,f1,f92,f93
  f92: plane 15.08x9.31mm, normal (0.85,0,-0.53), area 35.4mm2, adj f0,f1,f91,f93
  f93: cylinder r=20mm len=18.61mm, axis (0,-1,0), area 38.7mm2, adj f0,f1,f91,f92
  f94: plane 6.39x3.94mm, normal (-0.85,0,-0.53), area 15mm2, adj f0,f1,f95,f97
  f95: cylinder r=30mm len=49.56mm, axis (0,-1,0), area 116.6mm2, adj f0,f1,f94,f96
  f96: plane 6.39x3.94mm, normal (-0.85,0,0.53), area 15mm2, adj f0,f1,f95,f97
  f97: cylinder r=22.5mm len=36.78mm, axis (0,-1,0), area 86.1mm2, adj f0,f1,f94,f96
PLACE A t=(-153.89,-200.55,192.17)mm
PLACE B rot(axis=(0,0,1),180deg) t=(4.49,-254.55,211.86)mm
MATE slider A.f76 <-> B.f8  axis (0,-1,0) through (-90.39,-252.55,86.17)mm
